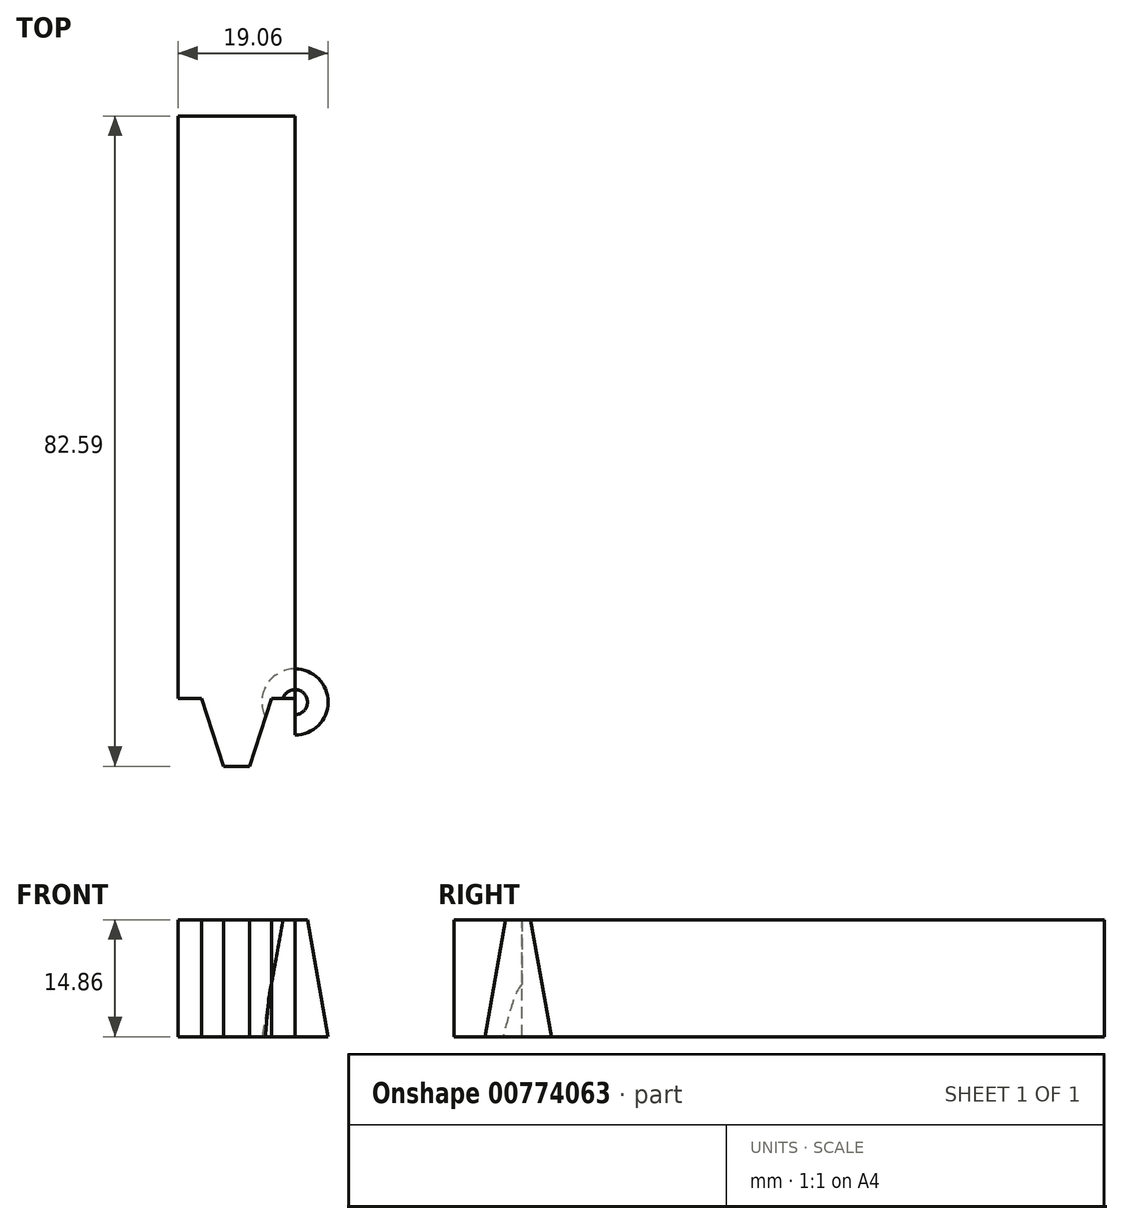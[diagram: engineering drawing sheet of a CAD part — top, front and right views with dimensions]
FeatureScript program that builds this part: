
annotation { "Feature Type Name" : "Feature", "Feature Type Description" : "" }
export const myFeature = defineFeature(function(context is Context, id is Id, definition is map)
    precondition{}
    {
        {
            assignVariable(context, id + "F0", {"name" : "tip_l", "anyValue" : 5 / 203.2 * mm});
        }
        {
            assignVariable(context, id + "F1", {"name" : "extra_l", "anyValue" : 3 / 203.2 * mm});
        }
        {
            assignVariable(context, id + "F2", {"name" : "toolholder_l", "anyValue" : 82.55 * mm});
        }
        {
            assignVariable(context, id + "F3", {"name" : "l", "anyValue" : getVariable(context, 'toolholder_l') + getVariable(context, 'tip_l') + getVariable(context, 'extra_l')});
        }
        {
            var Q0;
            Q0=qCreatedBy(makeId("Front.planeOp"),FACE);
            var sketch = newSketch(context, id + "F4", { "sketchPlane" : qUnion([Q0])});
            skLineSegment(sketch, "E0.bottom", {"start": v(45.82, 19.2) * mm, "end": v(30.96, 19.2) * mm});
            skLineSegment(sketch, "E0.top", {"start": v(45.82, 34.06) * mm, "end": v(30.96, 34.06) * mm});
            skLineSegment(sketch, "E0.left", {"start": v(45.82, 19.2) * mm, "end": v(45.82, 34.06) * mm});
            skLineSegment(sketch, "E0.right", {"start": v(30.96, 19.2) * mm, "end": v(30.96, 34.06) * mm});
            skPoint(sketch, "E0.middle", {"position": v(38.39, 26.63) * mm});
            skSolve(sketch);
        }
        {
            var Q0;
            Q0 = qSketchRegion(id + "F4", true);
            extrude(context, id + "F5", {"entities" : qUnion([Q0]), "oppositeDirection" : true, "depth" : getVariable(context, 'l'), "offsetDistance" : 25.4 * mm});
        }
        {
            var Q0;
            Q0=makeQuery(id+"F5.opExtrude","SWEPT_FACE",FACE,{"disambiguationData":[OSD([sQuery(id+"F4.wireOp",EDGE,"E0.top")])]});
            var sketch = newSketch(context, id + "F6", { "sketchPlane" : qUnion([Q0])});
            skLineSegment(sketch, "E1.0.0", {"start": v(30.96, 0) * mm, "end": v(45.82, 0) * mm, "construction": true});
            skLineSegment(sketch, "E1.0.1", {"start": v(45.82, 0) * mm, "end": v(45.82, 107.95) * mm, "construction": true});
            skLineSegment(sketch, "E1.0.2", {"start": v(45.82, 107.95) * mm, "end": v(30.96, 107.95) * mm, "construction": true});
            skLineSegment(sketch, "E1.0.3", {"start": v(30.96, 107.95) * mm, "end": v(30.96, 0) * mm, "construction": true});
            skLineSegment(sketch, "E2", {"start": v(36.75, 0) * mm, "end": v(40.03, 0) * mm});
            skLineSegment(sketch, "E3", {"start": v(40.03, 0) * mm, "end": v(42.83, 8.64) * mm});
            skLineSegment(sketch, "E4", {"start": v(42.83, 8.64) * mm, "end": v(45.82, 8.64) * mm});
            skLineSegment(sketch, "E5", {"start": v(38.39, 0) * mm, "end": v(38.39, 8.64) * mm, "construction": true});
            skLineSegment(sketch, "E6", {"start": v(36.75, 0) * mm, "end": v(33.94, 8.64) * mm});
            skLineSegment(sketch, "E7", {"start": v(33.94, 8.64) * mm, "end": v(30.96, 8.64) * mm});
            skSolve(sketch);
        }
        {
            var Q0;
            Q0=makeQuery(id+"F5.opExtrude","SWEPT_FACE",FACE,{"disambiguationData":[OSD([sQuery(id+"F4.wireOp",EDGE,"E0.top")])]});
            var sketch = newSketch(context, id + "F7", { "sketchPlane" : qUnion([Q0])});
            skCircle(sketch, "E8", {"center": v(45.82, 8.15) * mm, "radius": 1.59 * mm});
            skLineSegment(sketch, "E9", {"start": v(45.82, 8.15) * mm, "end": v(44.34, 8.15) * mm, "construction": true});
            skLineSegment(sketch, "E10.0", {"start": v(42.83, 8.64) * mm, "end": v(45.82, 8.64) * mm, "construction": true});
            skLineSegment(sketch, "E11.0", {"start": v(40.03, 0) * mm, "end": v(42.83, 8.64) * mm, "construction": true});
            skPoint(sketch, "E12.0", {"position": v(42.83, 8.64) * mm});
            skCircle(sketch, "E13", {"center": v(44.34, 8.15) * mm, "radius": 1.59 * mm, "construction": true});
            skSolve(sketch);
        }
        {
            var Q0;
            Q0=makeQuery(id+"F5.opExtrude","SWEPT_FACE",FACE,{"disambiguationData":[OSD([sQuery(id+"F4.wireOp",EDGE,"E0.left")])]});
            var sketch = newSketch(context, id + "F8", { "sketchPlane" : qUnion([Q0])});
            skLineSegment(sketch, "E14", {"start": v(9.73, 34.06) * mm, "end": v(8.15, 34.06) * mm});
            skLineSegment(sketch, "E15", {"start": v(6.56, 34.06) * mm, "end": v(3.94, 19.2) * mm, "construction": true});
            skLineSegment(sketch, "E16", {"start": v(3.94, 19.2) * mm, "end": v(8.15, 19.2) * mm, "construction": true});
            skLineSegment(sketch, "E17", {"start": v(12.35, 19.2) * mm, "end": v(9.73, 34.06) * mm});
            skLineSegment(sketch, "E18", {"start": v(8.15, 34.06) * mm, "end": v(8.15, 19.2) * mm});
            skLineSegment(sketch, "E19", {"start": v(8.15, 34.06) * mm, "end": v(6.56, 34.06) * mm, "construction": true});
            skLineSegment(sketch, "E20", {"start": v(8.15, 19.2) * mm, "end": v(12.35, 19.2) * mm});
            skSolve(sketch);
        }
        {
            var Q0;
            Q0=makeQuery(id+"F8.imprint","IMPRINT",FACE,{"disambiguationData":[TD([[makeQuery(id+"F8.imprint","IMPRINT",EDGE,{"derivedFrom":sQuery(id+"F8.wireOp",EDGE,"E14")}),1.0]])]});
            var Q1;
            Q1=sQuery(id+"F8.wireOp",EDGE,"E18");
            revolve(context, id + "F9", {"surfaceOperationType" : NewSurfaceOperationType.NEW, "entities" : qUnion([Q0]), "axis" : qUnion([Q1]), "revolveType" : RevolveType.FULL});
        }
        {
            var Q0;
            {var subQ0=sQuery(id+"F6.wireOp",EDGE,"E6");Q0=makeQuery(id+"F6.imprint","IMPRINT",FACE,{"disambiguationData":[TD([[makeQuery(id+"F6.imprint","IMPRINT",EDGE,{"derivedFrom":subQ0}),1.0]])]});}
            var Q1;
            {var subQ0=sQuery(id+"F6.wireOp",EDGE,"E3");Q1=makeQuery(id+"F6.imprint","IMPRINT",FACE,{"disambiguationData":[TD([[makeQuery(id+"F6.imprint","IMPRINT",EDGE,{"derivedFrom":subQ0}),-1.0]])]});}
            var Q2;
            Q2=makeQuery(id+"F5.opExtrude","SWEPT_FACE",FACE,{"disambiguationData":[OSD([sQuery(id+"F4.wireOp",EDGE,"E0.bottom")])]});
            extrude(context, id + "F10", {"entities" : qUnion([Q0, Q1]), "operationType" : NewBodyOperationType.REMOVE, "endBound" : BoundingType.UP_TO_SURFACE, "oppositeDirection" : true, "depth" : 25.4 * mm, "endBoundEntityFace" : qUnion([Q2]), "offsetDistance" : 25.4 * mm});
        }
    });
